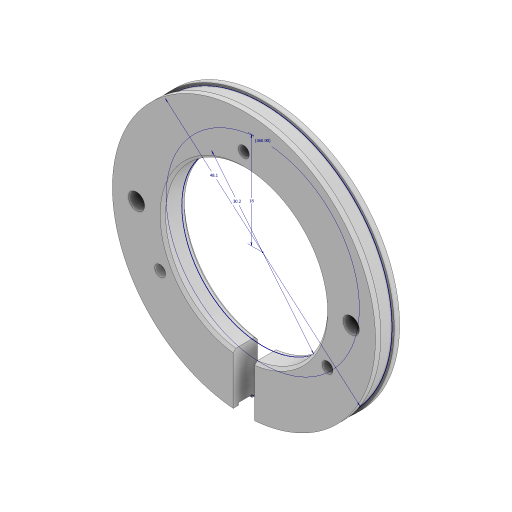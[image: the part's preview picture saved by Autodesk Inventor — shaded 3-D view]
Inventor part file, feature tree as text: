
AUTODESK INVENTOR PART (.ipt)
format: ipt  version: 2023 (Build 270158000, 158)  size: 188,416 bytes
history: native  units: mm
features: sketch x5, extrude x4, hole x2, chamfer x1
ambient origin geometry x8: Origin, YZ Plane, XZ Plane, XY Plane, X Axis, Y Axis, Z Axis, Center Point
bodies: Solid1 (feature_tree)
feature tree (12):
  sketch  "Sketch1"  dims[d1=48.1mm d2=18.0mm]
  extrude  "Extrusion1"  Depth=18.0mm
  hole  "Hole1"  [1 undecoded]
  extrude  "Extrusion2"  Depth=49.0mm
  extrude  "Extrusion3"  Depth=1.0mm TaperAngle=0.0deg
  extrude  "Extrusion4"  Depth=4.0mm
  hole  "Hole2"  [1 undecoded]
  chamfer  "Chamfer1"  [1 undecoded]
  sketch  "Sketch2"  dims[d3=30.0mm d5=360.0deg d7=2.5mm d8=0.0mm]
  sketch  "Sketch3"  dims[d9=2.0mm d10=6.0mm d11=4.0mm d12=2.0mm d13=90.0deg d14=8.0mm d15=20.594885mm d16=49.0mm]
  sketch  "Sketch4"  dims[d17=1.0mm d18=0.0mm d19=1.0mm d20=0.0mm]
  sketch  "Sketch5"  dims[d21=49.0mm d22=4.0mm d23=20.0mm d24=0.0mm d25=0.0mm d26=3.0mm d27=6.0mm d28=4.0mm d29=2.0mm d30=90.0deg d31=8.0mm d32=20.594885mm d33=0.0mm d34=0.5mm d35=2.0mm d36=45.0deg]
note: 3 required parameter values undecoded (feature->parameter linkage not recoverable at this tier; creation-order binding heuristic only, values carry confidence <= 0.55)
